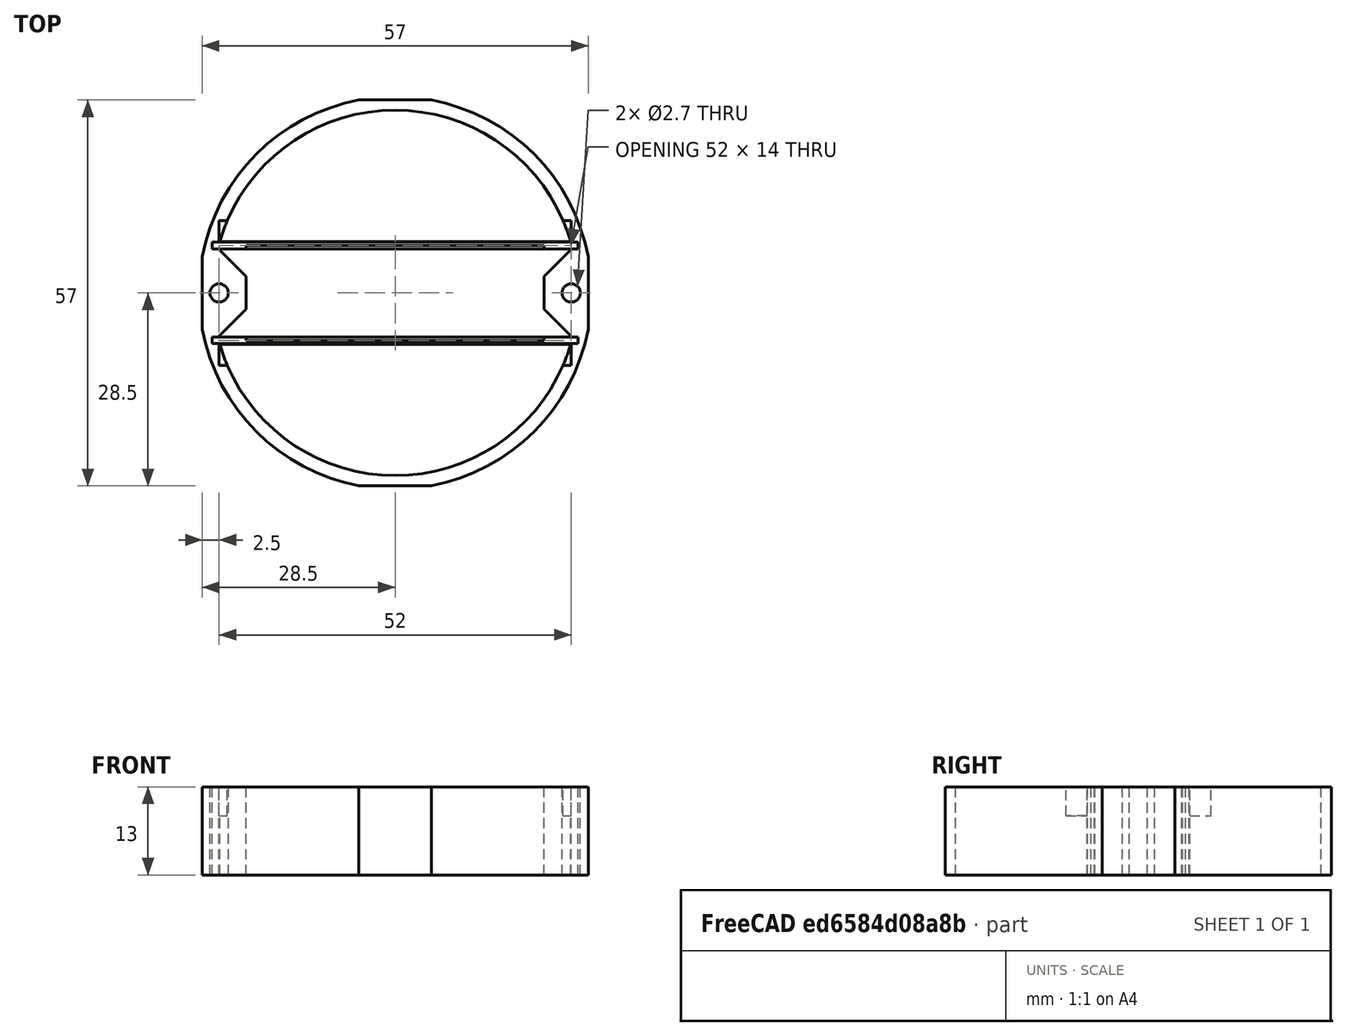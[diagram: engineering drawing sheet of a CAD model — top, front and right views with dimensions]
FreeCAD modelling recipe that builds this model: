
FCSTD DOCUMENT  (FreeCAD 0.16R)
Label: edizio_part_3_90grad
License: All rights reserved
LicenseURL: http://en.wikipedia.org/wiki/All_rights_reserved
objects: Part::Cut×13, Part::Box×12, Part::Cylinder×5, Part::Chamfer×4, Part::Common×1
note: 35 computed .brp shape members not serialized (recipe doc carries the construction recipe); baked Part::Feature solids carry a one-line shape summary decoded from their .brp

FEATURE [Part::Cylinder] Cylinder
  Angle = 360
  Height = 13
  Radius = 29
FEATURE [Part::Box] Box  label="Cube"
  Height = 13
  Length = 57
  Placement = pos=(-28.5,-28.5,0) rot=(0,0,1;0rad)
  Width = 57
FEATURE [Part::Common] Common
  Base = -> Cylinder
  Tool = -> Box
FEATURE [Part::Cylinder] Cylinder001
  Angle = 360
  Height = 13
  Placement = pos=(26,0,0) rot=(0,0,1;0rad)
  Radius = 1.35
FEATURE [Part::Cylinder] Cylinder002
  Angle = 360
  Height = 13
  Placement = pos=(-26,0,0) rot=(0,0,1;0rad)
  Radius = 1.35
FEATURE [Part::Cut] Cut
  Base = -> Common
  Tool = -> Cylinder001
FEATURE [Part::Cut] Cut001
  Base = -> Cut
  Tool = -> Cylinder002
FEATURE [Part::Box] Box001  label="Cube001"
  Height = 4.3
  Length = 52
  Placement = pos=(-26,7.6,8.75) rot=(0,0,1;0rad)
  Width = 3.1
FEATURE [Part::Box] Box002  label="Cube002"
  Height = 4.3
  Length = 52
  Placement = pos=(-26,-10.7,8.75) rot=(0,0,1;0rad)
  Width = 3.1
FEATURE [Part::Box] Box003  label="Cube003"
  Height = 13
  Length = 44
  Placement = pos=(-22,-7,0) rot=(0,0,1;0rad)
  Width = 14
FEATURE [Part::Cylinder] Cylinder003
  Angle = 360
  Height = 13
  Radius = 27
FEATURE [Part::Cylinder] Cylinder004
  Angle = 360
  Height = 13
  Radius = 27
FEATURE [Part::Box] Box004  label="Cube004"
  Height = 13
  Length = 60
  Placement = pos=(-30,-7.6,0) rot=(0,0,1;0rad)
  Width = 60
FEATURE [Part::Box] Box005  label="Cube005"
  Height = 13
  Length = 60
  Placement = pos=(-30,-52.4,0) rot=(0,0,1;0rad)
  Width = 60
FEATURE [Part::Cut] Cut002
  Base = -> Cylinder003
  Tool = -> Box004
FEATURE [Part::Cut] Cut003
  Base = -> Cylinder004
  Tool = -> Box005
FEATURE [Part::Cut] Cut004
  Base = -> Cut001
  Tool = -> Cut002
FEATURE [Part::Cut] Cut005
  Base = -> Cut004
  Tool = -> Cut003
FEATURE [Part::Cut] Cut006
  Base = -> Cut005
  Tool = -> Box001
FEATURE [Part::Cut] Cut007
  Base = -> Cut006
  Tool = -> Box002
FEATURE [Part::Cut] Cut008
  Base = -> Cut007
  Tool = -> Box003
FEATURE [Part::Box] Box006  label="Cube006"
  Height = 13
  Length = 5
  Width = 5
FEATURE [Part::Chamfer] Chamfer
  Base = -> Box006
  Edges = 1 edges r=4.9: [Edge1]
  Placement = pos=(-26,1.5,0) rot=(0,0,1;0rad)
FEATURE [Part::Box] Box007  label="Cube007"
  Height = 13
  Length = 54
  Placement = pos=(-27,6.5,0) rot=(0,0,1;0rad)
  Width = 1
FEATURE [Part::Box] Box008  label="Cube008"
  Height = 13
  Length = 54
  Placement = pos=(-27,-7.5,0) rot=(0,0,1;0rad)
  Width = 1
FEATURE [Part::Box] Box009  label="Cube009"
  Height = 13
  Length = 5
  Width = 5
FEATURE [Part::Chamfer] Chamfer001
  Base = -> Box009
  Edges = 1 edges r=4.9: [Edge1]
  Placement = pos=(26,1.5,0) rot=(0,0,1;1.5708rad)
FEATURE [Part::Box] Box010  label="Cube010"
  Height = 13
  Length = 5
  Width = 5
FEATURE [Part::Chamfer] Chamfer002
  Base = -> Box010
  Edges = 1 edges r=4.9: [Edge1]
  Placement = pos=(26,-1.5,0) rot=(0,0,1;3.14159rad)
FEATURE [Part::Box] Box011  label="Cube011"
  Height = 13
  Length = 5
  Width = 5
FEATURE [Part::Chamfer] Chamfer003
  Base = -> Box011
  Edges = 1 edges r=4.9: [Edge1]
  Placement = pos=(-26,-1.5,0) rot=(0,0,1;4.71239rad)
FEATURE [Part::Cut] Cut009
  Base = -> Cut008
  Tool = -> Chamfer
FEATURE [Part::Cut] Cut010
  Base = -> Cut009
  Tool = -> Chamfer001
FEATURE [Part::Cut] Cut011
  Base = -> Cut010
  Tool = -> Chamfer002
FEATURE [Part::Cut] Cut012
  Base = -> Cut011
  Tool = -> Chamfer003
